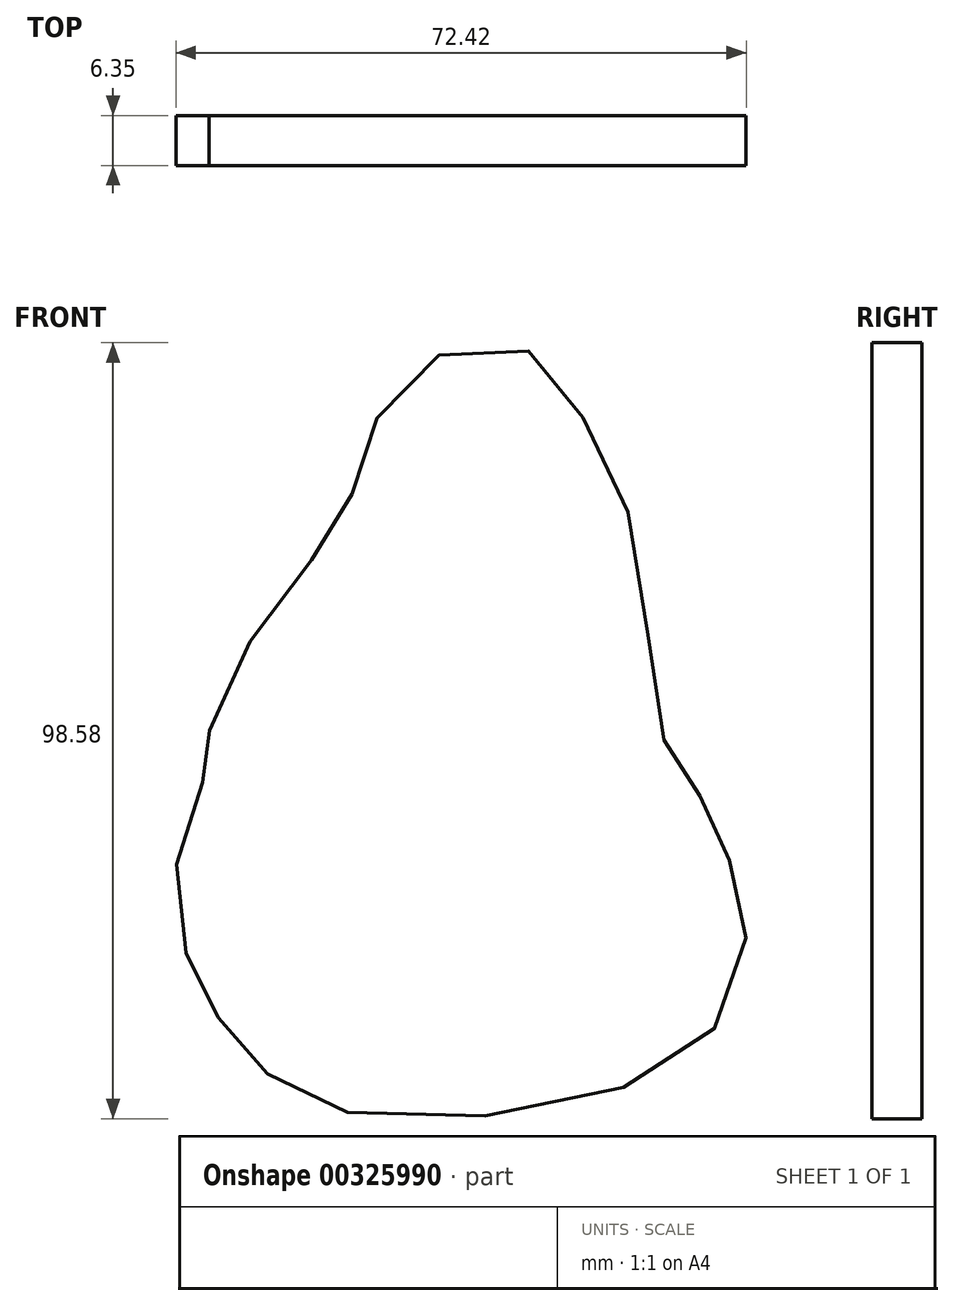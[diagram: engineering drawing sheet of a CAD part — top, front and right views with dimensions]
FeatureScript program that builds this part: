
annotation { "Feature Type Name" : "Feature", "Feature Type Description" : "" }
export const myFeature = defineFeature(function(context is Context, id is Id, definition is map)
    precondition{}
    {
        {
            var Q0;
            Q0=qCreatedBy(makeId("Front.planeOp"),FACE);
            var sketch = newSketch(context, id + "F0", { "sketchPlane" : qUnion([Q0])});
            skPoint(sketch, "E0.start.orphan", {"position": v(-36.55, 0) * mm});
            skFitSpline(sketch, "E1", {"points": [v(-27.63, 0) * mm, v(-19.86, 15.25) * mm, v(-11.51, 25.9) * mm, v(-8.06, 34.82) * mm, v(-2.59, 45.19) * mm, v(11.23, 48.93) * mm, v(19.29, 40.58) * mm, v(26.77, 23.02) * mm, v(29.64, 0) * mm, v(33.68, -6.62) * mm, v(37.13, -13.81) * mm, v(40.3, -22.45) * mm, v(37.42, -36.55) * mm, v(19.57, -46.91) * mm, v(-12.09, -48.06) * mm, v(-21.87, -42.02) * mm, v(-27.63, -34.82) * mm, v(-31.08, -26.48) * mm, v(-31.08, -12.66) * mm, v(-27.63, -4.03) * mm, v(-27.63, 0) * mm]});
            skSolve(sketch);
        }
        {
            var Q0;
            {var subQ0=sQuery(id+"F0.wireOp",EDGE,"J3PTCCj1-ht1T-KwEA-84up-VUIEAyjodGVO");Q0=makeQuery(id+"F0.imprint","IMPRINT",FACE,{"disambiguationData":[TD([[makeQuery(id+"F0.imprint","IMPRINT",EDGE,{"derivedFrom":subQ0}),-1.0]])]});}
            var Q1;
            {var subQ0=sQuery(id+"F0.wireOp",EDGE,"J3PTCCj1-ht1T-KwEA-84up-VUIEAyjodGVO");Q1=makeQuery(id+"F0.imprint","IMPRINT",FACE,{"disambiguationData":[TD([[makeQuery(id+"F0.imprint","IMPRINT",EDGE,{"derivedFrom":subQ0}),1.0]])]});}
            var Q2;
            Q2=makeQuery(id+"F0.imprint","IMPRINT",FACE,{"disambiguationData":[TD([[makeQuery(id+"F0.imprint","IMPRINT",EDGE,{"derivedFrom":sQuery(id+"F0.wireOp",EDGE,"E1")}),-1.0]])]});
            extrude(context, id + "F1", {"entities" : qUnion([Q0, Q1, Q2]), "depth" : 6.35 * mm});
        }
    });
